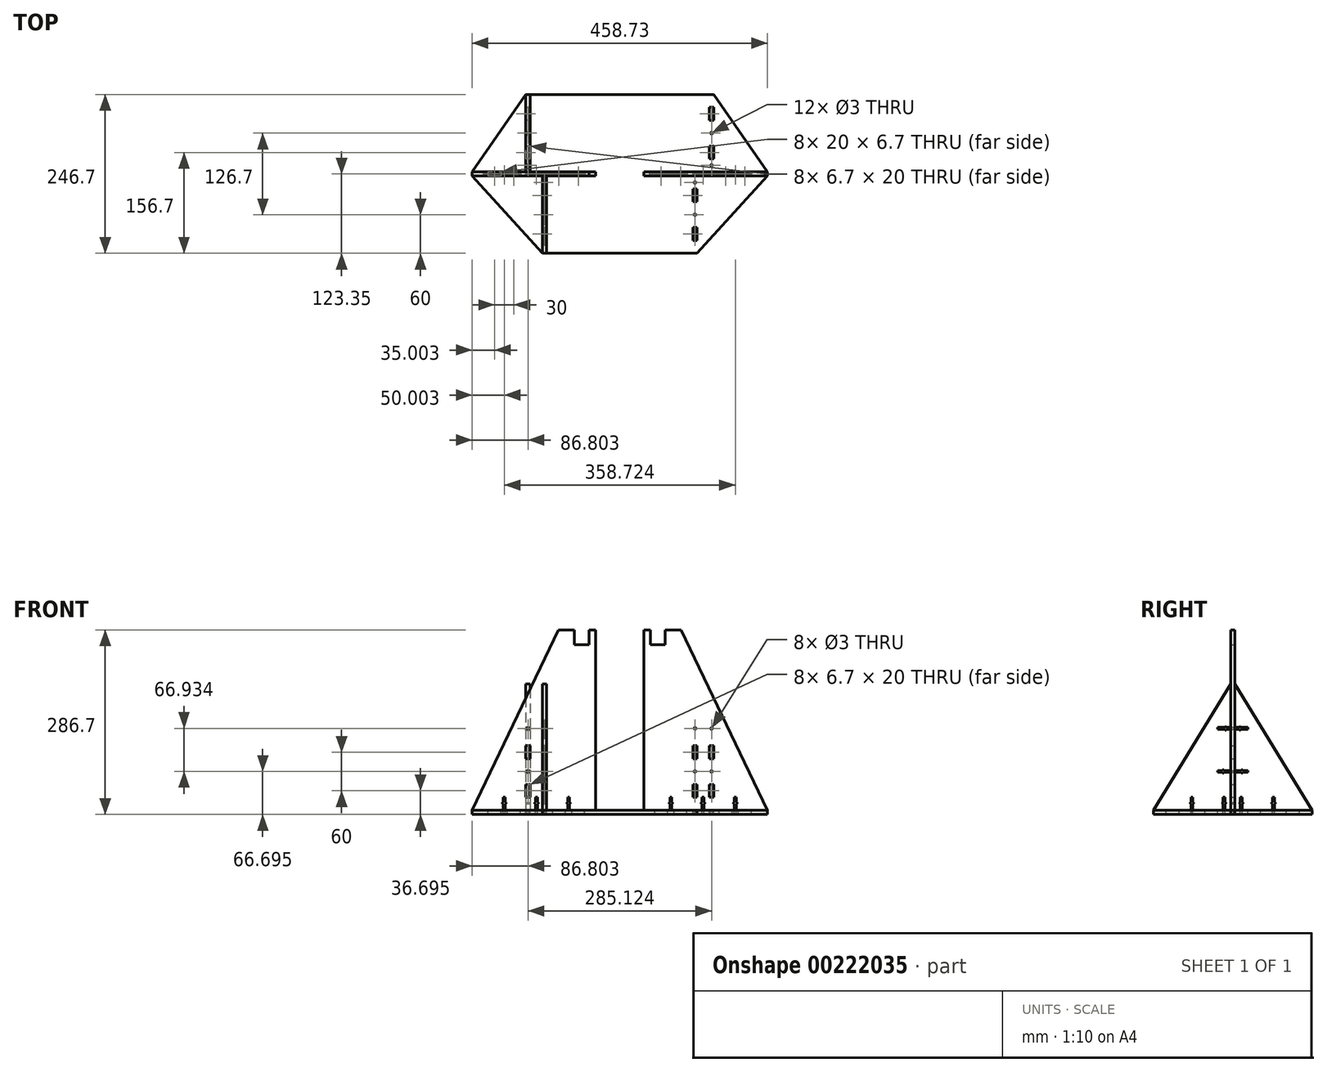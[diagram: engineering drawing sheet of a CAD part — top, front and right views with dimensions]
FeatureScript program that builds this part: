
annotation { "Feature Type Name" : "Feature", "Feature Type Description" : "" }
export const myFeature = defineFeature(function(context is Context, id is Id, definition is map)
    precondition{}
    {
        {
            var Q0;
            Q0=qCreatedBy(makeId("Front.planeOp"),FACE);
            var sketch = newSketch(context, id + "F0", { "sketchPlane" : qUnion([Q0])});
            skLineSegment(sketch, "E0", {"start": v(-65.14, 306.1) * mm, "end": v(-65.14, 283.1) * mm});
            skLineSegment(sketch, "E1", {"start": v(-65.14, 306.1) * mm, "end": v(-55.14, 306.1) * mm, "construction": true});
            skLineSegment(sketch, "E2", {"start": v(-65.14, 283.1) * mm, "end": v(-88.14, 283.1) * mm});
            skLineSegment(sketch, "E3", {"start": v(-88.14, 283.1) * mm, "end": v(-88.14, 306.1) * mm});
            skLineSegment(sketch, "E4", {"start": v(-65.14, 306.1) * mm, "end": v(-55.14, 306.1) * mm});
            skLineSegment(sketch, "E5", {"start": v(-88.14, 306.1) * mm, "end": v(-113.14, 306.1) * mm});
            skLineSegment(sketch, "E6", {"start": v(-113.14, 306.1) * mm, "end": v(-247, 26.1) * mm});
            skLineSegment(sketch, "E7", {"start": v(-247, 26.1) * mm, "end": v(-222, 26.1) * mm});
            skLineSegment(sketch, "E8.top", {"start": v(-222, 19.4) * mm, "end": v(-202, 19.4) * mm});
            skLineSegment(sketch, "E8.left", {"start": v(-222, 26.1) * mm, "end": v(-222, 19.4) * mm});
            skLineSegment(sketch, "E8.right", {"start": v(-202, 26.1) * mm, "end": v(-202, 19.4) * mm});
            skLineSegment(sketch, "E9.top", {"start": v(-192, 19.4) * mm, "end": v(-172, 19.4) * mm});
            skLineSegment(sketch, "E9.left", {"start": v(-192, 26.1) * mm, "end": v(-192, 19.4) * mm});
            skLineSegment(sketch, "E9.right", {"start": v(-172, 26.1) * mm, "end": v(-172, 19.4) * mm});
            skLineSegment(sketch, "E10.trimOffspring", {"start": v(-202, 26.1) * mm, "end": v(-198.5, 26.1) * mm});
            skLineSegment(sketch, "E11.MirrorCS", {"start": v(-122, 26.1) * mm, "end": v(-122, 19.4) * mm});
            skLineSegment(sketch, "E12.MirrorCS", {"start": v(-102, 19.4) * mm, "end": v(-122, 19.4) * mm});
            skLineSegment(sketch, "E13.MirrorCS", {"start": v(-102, 26.1) * mm, "end": v(-102, 19.4) * mm});
            skLineSegment(sketch, "E14.MirrorCS", {"start": v(-92, 26.1) * mm, "end": v(-95.5, 26.1) * mm});
            skLineSegment(sketch, "E15.MirrorCS", {"start": v(-92, 26.1) * mm, "end": v(-92, 19.4) * mm});
            skLineSegment(sketch, "E16.MirrorCS", {"start": v(-72, 26.1) * mm, "end": v(-72, 19.4) * mm});
            skLineSegment(sketch, "E17.MirrorCS", {"start": v(-72, 19.4) * mm, "end": v(-92, 19.4) * mm});
            skLineSegment(sketch, "E18", {"start": v(-72, 26.1) * mm, "end": v(-55.14, 26.1) * mm});
            skLineSegment(sketch, "E19.bottom", {"start": v(-198.5, 46.1) * mm, "end": v(-195.5, 46.1) * mm});
            skLineSegment(sketch, "E19.left", {"start": v(-198.5, 46.1) * mm, "end": v(-198.5, 37.9) * mm});
            skLineSegment(sketch, "E19.right", {"start": v(-195.5, 46.1) * mm, "end": v(-195.5, 37.9) * mm});
            skPoint(sketch, "E20.oppositeSnap0", {"position": v(-195.5, 36.1) * mm});
            skLineSegment(sketch, "E20.bottom", {"start": v(-199.76, 37.9) * mm, "end": v(-198.5, 37.9) * mm});
            skLineSegment(sketch, "E20.top", {"start": v(-199.76, 36.1) * mm, "end": v(-198.5, 36.1) * mm});
            skLineSegment(sketch, "E20.left", {"start": v(-199.76, 37.9) * mm, "end": v(-199.76, 36.1) * mm});
            skLineSegment(sketch, "E20.right", {"start": v(-194.26, 37.9) * mm, "end": v(-194.26, 36.1) * mm});
            skLineSegment(sketch, "E21.trimOffspring", {"start": v(-195.5, 36.1) * mm, "end": v(-194.26, 36.1) * mm});
            skLineSegment(sketch, "E22.trimOffspring", {"start": v(-195.5, 37.9) * mm, "end": v(-194.26, 37.9) * mm});
            skLineSegment(sketch, "E23.trimOffspring", {"start": v(-198.5, 36.1) * mm, "end": v(-198.5, 26.1) * mm});
            skLineSegment(sketch, "E24.trimOffspring", {"start": v(-195.5, 36.1) * mm, "end": v(-195.5, 26.1) * mm});
            skLineSegment(sketch, "E25.trimOffspring", {"start": v(-195.5, 26.1) * mm, "end": v(-192, 26.1) * mm});
            skLineSegment(sketch, "E26.MirrorCS", {"start": v(-95.5, 46.1) * mm, "end": v(-98.5, 46.1) * mm});
            skLineSegment(sketch, "E27.MirrorCS", {"start": v(-98.5, 46.1) * mm, "end": v(-98.5, 37.9) * mm});
            skLineSegment(sketch, "E28.MirrorCS", {"start": v(-98.5, 37.9) * mm, "end": v(-99.76, 37.9) * mm});
            skLineSegment(sketch, "E29.MirrorCS", {"start": v(-99.76, 37.9) * mm, "end": v(-99.76, 36.1) * mm});
            skLineSegment(sketch, "E30.MirrorCS", {"start": v(-98.5, 36.1) * mm, "end": v(-99.76, 36.1) * mm});
            skLineSegment(sketch, "E31.MirrorCS", {"start": v(-98.5, 36.1) * mm, "end": v(-98.5, 26.1) * mm});
            skLineSegment(sketch, "E32.MirrorCS", {"start": v(-94.26, 37.9) * mm, "end": v(-95.5, 37.9) * mm});
            skLineSegment(sketch, "E33.MirrorCS", {"start": v(-95.5, 46.1) * mm, "end": v(-95.5, 37.9) * mm});
            skLineSegment(sketch, "E34.MirrorCS", {"start": v(-94.26, 37.9) * mm, "end": v(-94.26, 36.1) * mm});
            skLineSegment(sketch, "E35.MirrorCS", {"start": v(-95.5, 36.1) * mm, "end": v(-95.5, 26.1) * mm});
            skLineSegment(sketch, "E36.MirrorCS", {"start": v(-94.26, 36.1) * mm, "end": v(-95.5, 36.1) * mm});
            skLineSegment(sketch, "E37.trimOffspring", {"start": v(-98.5, 26.1) * mm, "end": v(-102, 26.1) * mm});
            skLineSegment(sketch, "E38.bottom", {"start": v(-163.56, 126.1) * mm, "end": v(-156.86, 126.1) * mm, "construction": true});
            skLineSegment(sketch, "E39.bottom", {"start": v(-163.56, 126.1) * mm, "end": v(-156.86, 126.1) * mm});
            skLineSegment(sketch, "E39.top", {"start": v(-163.56, 106.1) * mm, "end": v(-156.86, 106.1) * mm});
            skLineSegment(sketch, "E39.left", {"start": v(-163.56, 126.1) * mm, "end": v(-163.56, 106.1) * mm});
            skLineSegment(sketch, "E39.right", {"start": v(-156.86, 126.1) * mm, "end": v(-156.86, 106.1) * mm});
            skLineSegment(sketch, "E40.bottom", {"start": v(-156.86, 66.1) * mm, "end": v(-163.56, 66.1) * mm});
            skLineSegment(sketch, "E40.top", {"start": v(-156.86, 46.1) * mm, "end": v(-163.56, 46.1) * mm});
            skLineSegment(sketch, "E40.left", {"start": v(-156.86, 66.1) * mm, "end": v(-156.86, 46.1) * mm});
            skLineSegment(sketch, "E40.right", {"start": v(-163.56, 66.1) * mm, "end": v(-163.56, 46.1) * mm});
            skCircle(sketch, "E41", {"center": v(-160.2, 86.1) * mm, "radius": 1.5 * mm});
            skLineSegment(sketch, "E42.bottom", {"start": v(-137.86, 126.1) * mm, "end": v(-131.16, 126.1) * mm});
            skLineSegment(sketch, "E42.top", {"start": v(-137.86, 106.1) * mm, "end": v(-131.16, 106.1) * mm});
            skLineSegment(sketch, "E42.left", {"start": v(-137.86, 126.1) * mm, "end": v(-137.86, 106.1) * mm});
            skLineSegment(sketch, "E42.right", {"start": v(-131.16, 126.1) * mm, "end": v(-131.16, 106.1) * mm});
            skCircle(sketch, "E43", {"center": v(-134.5, 86.1) * mm, "radius": 1.5 * mm});
            skLineSegment(sketch, "E44.bottom", {"start": v(-137.86, 66.1) * mm, "end": v(-131.16, 66.1) * mm});
            skLineSegment(sketch, "E44.top", {"start": v(-137.86, 46.1) * mm, "end": v(-131.16, 46.1) * mm});
            skLineSegment(sketch, "E44.left", {"start": v(-137.86, 66.1) * mm, "end": v(-137.86, 46.1) * mm});
            skLineSegment(sketch, "E44.right", {"start": v(-131.16, 66.1) * mm, "end": v(-131.16, 46.1) * mm});
            skLineSegment(sketch, "E45", {"start": v(-122, 26.1) * mm, "end": v(-145.5, 26.1) * mm});
            skLineSegment(sketch, "E46.bottom", {"start": v(-148.5, 46.1) * mm, "end": v(-145.5, 46.1) * mm});
            skLineSegment(sketch, "E46.left", {"start": v(-148.5, 46.1) * mm, "end": v(-148.5, 37.9) * mm});
            skLineSegment(sketch, "E46.right", {"start": v(-145.5, 46.1) * mm, "end": v(-145.5, 37.9) * mm});
            skLineSegment(sketch, "E47.bottom", {"start": v(-149.76, 37.9) * mm, "end": v(-148.5, 37.9) * mm});
            skLineSegment(sketch, "E47.top", {"start": v(-149.76, 36.1) * mm, "end": v(-148.5, 36.1) * mm});
            skLineSegment(sketch, "E47.left", {"start": v(-149.76, 37.9) * mm, "end": v(-149.76, 36.1) * mm});
            skLineSegment(sketch, "E47.right", {"start": v(-144.26, 37.9) * mm, "end": v(-144.26, 36.1) * mm});
            skLineSegment(sketch, "E48.trimOffspring", {"start": v(-145.5, 36.1) * mm, "end": v(-144.26, 36.1) * mm});
            skLineSegment(sketch, "E49.trimOffspring", {"start": v(-148.5, 36.1) * mm, "end": v(-148.5, 26.1) * mm});
            skLineSegment(sketch, "E50.trimOffspring", {"start": v(-145.5, 37.9) * mm, "end": v(-144.26, 37.9) * mm});
            skLineSegment(sketch, "E51.trimOffspring", {"start": v(-145.5, 36.1) * mm, "end": v(-145.5, 26.1) * mm});
            skLineSegment(sketch, "E52.trimOffspring", {"start": v(-148.5, 26.1) * mm, "end": v(-172, 26.1) * mm});
            skLineSegment(sketch, "E53.MirrorCS", {"start": v(158.97, 37.9) * mm, "end": v(158.97, 36.1) * mm});
            skLineSegment(sketch, "E54.MirrorCS", {"start": v(164.47, 37.9) * mm, "end": v(163.22, 37.9) * mm});
            skLineSegment(sketch, "E55.MirrorCS", {"start": v(160.22, 36.1) * mm, "end": v(158.97, 36.1) * mm});
            skLineSegment(sketch, "E56.MirrorCS", {"start": v(164.47, 37.9) * mm, "end": v(164.47, 36.1) * mm});
            skLineSegment(sketch, "E57.MirrorCS", {"start": v(160.22, 37.9) * mm, "end": v(158.97, 37.9) * mm});
            skLineSegment(sketch, "E58.MirrorCS", {"start": v(164.47, 36.1) * mm, "end": v(163.22, 36.1) * mm});
            skLineSegment(sketch, "E59.MirrorCS", {"start": v(63.22, 37.9) * mm, "end": v(64.47, 37.9) * mm});
            skLineSegment(sketch, "E60.MirrorCS", {"start": v(63.22, 36.1) * mm, "end": v(64.47, 36.1) * mm});
            skLineSegment(sketch, "E61.MirrorCS", {"start": v(64.47, 37.9) * mm, "end": v(64.47, 36.1) * mm});
            skLineSegment(sketch, "E62.MirrorCS", {"start": v(58.97, 36.1) * mm, "end": v(60.22, 36.1) * mm});
            skLineSegment(sketch, "E63.MirrorCS", {"start": v(58.97, 37.9) * mm, "end": v(58.97, 36.1) * mm});
            skLineSegment(sketch, "E64.MirrorCS", {"start": v(58.97, 37.9) * mm, "end": v(60.22, 37.9) * mm});
            skLineSegment(sketch, "E65.MirrorCS", {"start": v(108.97, 37.9) * mm, "end": v(108.97, 36.1) * mm});
            skLineSegment(sketch, "E66.MirrorCS", {"start": v(114.47, 36.1) * mm, "end": v(113.22, 36.1) * mm});
            skLineSegment(sketch, "E67.MirrorCS", {"start": v(114.47, 37.9) * mm, "end": v(113.22, 37.9) * mm});
            skLineSegment(sketch, "E68.MirrorCS", {"start": v(110.22, 37.9) * mm, "end": v(108.97, 37.9) * mm});
            skLineSegment(sketch, "E69.MirrorCS", {"start": v(110.22, 36.1) * mm, "end": v(108.97, 36.1) * mm});
            skLineSegment(sketch, "E70.MirrorCS", {"start": v(114.47, 37.9) * mm, "end": v(114.47, 36.1) * mm});
            skLineSegment(sketch, "E71.MirrorCS", {"start": v(160.22, 26.1) * mm, "end": v(156.72, 26.1) * mm});
            skLineSegment(sketch, "E72.MirrorCS", {"start": v(56.72, 26.1) * mm, "end": v(60.22, 26.1) * mm});
            skLineSegment(sketch, "E73.MirrorCS", {"start": v(166.72, 26.1) * mm, "end": v(163.22, 26.1) * mm});
            skLineSegment(sketch, "E74.MirrorCS", {"start": v(128.27, 126.1) * mm, "end": v(121.57, 126.1) * mm});
            skLineSegment(sketch, "E75.MirrorCS", {"start": v(63.22, 26.1) * mm, "end": v(66.72, 26.1) * mm});
            skLineSegment(sketch, "E76.MirrorCS", {"start": v(156.72, 26.1) * mm, "end": v(156.72, 19.4) * mm});
            skLineSegment(sketch, "E77.MirrorCS", {"start": v(66.72, 26.1) * mm, "end": v(66.72, 19.4) * mm});
            skLineSegment(sketch, "E78.MirrorCS", {"start": v(63.22, 36.1) * mm, "end": v(63.22, 26.1) * mm});
            skLineSegment(sketch, "E79.MirrorCS", {"start": v(29.86, 306.1) * mm, "end": v(19.86, 306.1) * mm, "construction": true});
            skLineSegment(sketch, "E80.MirrorCS", {"start": v(128.27, 126.1) * mm, "end": v(121.57, 126.1) * mm, "construction": true});
            skLineSegment(sketch, "E81.MirrorCS", {"start": v(166.72, 26.1) * mm, "end": v(166.72, 19.4) * mm});
            skLineSegment(sketch, "E82.MirrorCS", {"start": v(110.22, 46.1) * mm, "end": v(110.22, 37.9) * mm});
            skLineSegment(sketch, "E83.MirrorCS", {"start": v(56.72, 26.1) * mm, "end": v(56.72, 19.4) * mm});
            skLineSegment(sketch, "E84.MirrorCS", {"start": v(160.22, 36.1) * mm, "end": v(160.22, 26.1) * mm});
            skLineSegment(sketch, "E85.MirrorCS", {"start": v(60.22, 36.1) * mm, "end": v(60.22, 26.1) * mm});
            skLineSegment(sketch, "E86.MirrorCS", {"start": v(113.22, 46.1) * mm, "end": v(110.22, 46.1) * mm});
            skLineSegment(sketch, "E87.MirrorCS", {"start": v(163.22, 36.1) * mm, "end": v(163.22, 26.1) * mm});
            skLineSegment(sketch, "E88.MirrorCS", {"start": v(113.22, 46.1) * mm, "end": v(113.22, 37.9) * mm});
            skLineSegment(sketch, "E89.MirrorCS", {"start": v(128.27, 106.1) * mm, "end": v(121.57, 106.1) * mm});
            skLineSegment(sketch, "E90.MirrorCS", {"start": v(121.57, 46.1) * mm, "end": v(128.27, 46.1) * mm});
            skLineSegment(sketch, "E91.MirrorCS", {"start": v(160.22, 46.1) * mm, "end": v(160.22, 37.9) * mm});
            skLineSegment(sketch, "E92.MirrorCS", {"start": v(102.57, 126.1) * mm, "end": v(95.87, 126.1) * mm});
            skLineSegment(sketch, "E93.MirrorCS", {"start": v(163.22, 46.1) * mm, "end": v(163.22, 37.9) * mm});
            skLineSegment(sketch, "E94.MirrorCS", {"start": v(136.72, 26.1) * mm, "end": v(136.72, 19.4) * mm});
            skLineSegment(sketch, "E95.MirrorCS", {"start": v(163.22, 46.1) * mm, "end": v(160.22, 46.1) * mm});
            skLineSegment(sketch, "E96.MirrorCS", {"start": v(86.72, 26.1) * mm, "end": v(86.72, 19.4) * mm});
            skLineSegment(sketch, "E97.MirrorCS", {"start": v(186.72, 26.1) * mm, "end": v(186.72, 19.4) * mm});
            skLineSegment(sketch, "E98.MirrorCS", {"start": v(110.22, 36.1) * mm, "end": v(110.22, 26.1) * mm});
            skLineSegment(sketch, "E99.MirrorCS", {"start": v(121.57, 66.1) * mm, "end": v(128.27, 66.1) * mm});
            skLineSegment(sketch, "E100.MirrorCS", {"start": v(102.57, 106.1) * mm, "end": v(95.87, 106.1) * mm});
            skLineSegment(sketch, "E101.MirrorCS", {"start": v(102.57, 66.1) * mm, "end": v(95.87, 66.1) * mm});
            skLineSegment(sketch, "E102.MirrorCS", {"start": v(60.22, 46.1) * mm, "end": v(63.22, 46.1) * mm});
            skLineSegment(sketch, "E103.MirrorCS", {"start": v(102.57, 46.1) * mm, "end": v(95.87, 46.1) * mm});
            skLineSegment(sketch, "E104.MirrorCS", {"start": v(113.22, 36.1) * mm, "end": v(113.22, 26.1) * mm});
            skLineSegment(sketch, "E105.MirrorCS", {"start": v(60.22, 46.1) * mm, "end": v(60.22, 37.9) * mm});
            skLineSegment(sketch, "E106.MirrorCS", {"start": v(36.72, 26.1) * mm, "end": v(36.72, 19.4) * mm});
            skLineSegment(sketch, "E107.MirrorCS", {"start": v(63.22, 46.1) * mm, "end": v(63.22, 37.9) * mm});
            skCircle(sketch, "E108.MirrorC", {"center": v(124.92, 86.1) * mm, "radius": 1.5 * mm});
            skLineSegment(sketch, "E109.MirrorCS", {"start": v(29.86, 306.1) * mm, "end": v(19.86, 306.1) * mm});
            skCircle(sketch, "E110.MirrorC", {"center": v(99.22, 86.1) * mm, "radius": 1.5 * mm});
            skLineSegment(sketch, "E111.MirrorCS", {"start": v(156.72, 19.4) * mm, "end": v(136.72, 19.4) * mm});
            skLineSegment(sketch, "E112.MirrorCS", {"start": v(95.87, 126.1) * mm, "end": v(95.87, 106.1) * mm});
            skLineSegment(sketch, "E113.MirrorCS", {"start": v(128.27, 126.1) * mm, "end": v(128.27, 106.1) * mm});
            skLineSegment(sketch, "E114.MirrorCS", {"start": v(95.87, 66.1) * mm, "end": v(95.87, 46.1) * mm});
            skLineSegment(sketch, "E115.MirrorCS", {"start": v(29.86, 306.1) * mm, "end": v(29.86, 283.1) * mm});
            skLineSegment(sketch, "E116.MirrorCS", {"start": v(102.57, 66.1) * mm, "end": v(102.57, 46.1) * mm});
            skLineSegment(sketch, "E117.MirrorCS", {"start": v(29.86, 283.1) * mm, "end": v(52.86, 283.1) * mm});
            skLineSegment(sketch, "E118.MirrorCS", {"start": v(128.27, 66.1) * mm, "end": v(128.27, 46.1) * mm});
            skLineSegment(sketch, "E119.MirrorCS", {"start": v(52.86, 283.1) * mm, "end": v(52.86, 306.1) * mm});
            skLineSegment(sketch, "E120.MirrorCS", {"start": v(52.86, 306.1) * mm, "end": v(77.86, 306.1) * mm});
            skLineSegment(sketch, "E121.MirrorCS", {"start": v(77.86, 306.1) * mm, "end": v(211.72, 26.1) * mm});
            skLineSegment(sketch, "E122.MirrorCS", {"start": v(211.72, 26.1) * mm, "end": v(186.72, 26.1) * mm});
            skLineSegment(sketch, "E123.MirrorCS", {"start": v(121.57, 66.1) * mm, "end": v(121.57, 46.1) * mm});
            skLineSegment(sketch, "E124.MirrorCS", {"start": v(36.72, 26.1) * mm, "end": v(19.86, 26.1) * mm});
            skLineSegment(sketch, "E125.MirrorCS", {"start": v(66.72, 19.4) * mm, "end": v(86.72, 19.4) * mm});
            skLineSegment(sketch, "E126.MirrorCS", {"start": v(36.72, 19.4) * mm, "end": v(56.72, 19.4) * mm});
            skLineSegment(sketch, "E127.MirrorCS", {"start": v(113.22, 26.1) * mm, "end": v(136.72, 26.1) * mm});
            skLineSegment(sketch, "E128.MirrorCS", {"start": v(121.57, 126.1) * mm, "end": v(121.57, 106.1) * mm});
            skPoint(sketch, "E129.MirrorP", {"position": v(160.22, 36.1) * mm});
            skLineSegment(sketch, "E130.MirrorCS", {"start": v(186.72, 19.4) * mm, "end": v(166.72, 19.4) * mm});
            skLineSegment(sketch, "E131.MirrorCS", {"start": v(102.57, 126.1) * mm, "end": v(102.57, 106.1) * mm});
            skLineSegment(sketch, "E132.MirrorCS", {"start": v(86.72, 26.1) * mm, "end": v(110.22, 26.1) * mm});
            skPoint(sketch, "E133.endSnap0", {"position": v(-58.58, 26.1) * mm});
            skLineSegment(sketch, "E134", {"start": v(-55.14, 306.1) * mm, "end": v(-55.14, 26.1) * mm});
            skLineSegment(sketch, "E135.trimOffspring", {"start": v(-55.14, 306.1) * mm, "end": v(-65.14, 306.1) * mm, "construction": true});
            skLineSegment(sketch, "E136", {"start": v(19.86, 306.1) * mm, "end": v(19.86, 26.1) * mm});
            skPoint(sketch, "E136.startSnap0", {"position": v(19.86, 306.1) * mm});
            skLineSegment(sketch, "E137.trimOffspring", {"start": v(19.86, 306.1) * mm, "end": v(29.86, 306.1) * mm, "construction": true});
            skPoint(sketch, "E138.orphan", {"position": v(19.86, 315.9) * mm});
            skPoint(sketch, "E139.trimOffspring.start.orphan", {"position": v(9.86, 306.1) * mm});
            skSolve(sketch);
        }
        {
            var Q0;
            Q0 = qSketchRegion(id + "F0", true);
            extrude(context, id + "F1", {"entities" : qUnion([Q0]), "depth" : 6.7 * mm});
        }
        {
            var Q0;
            Q0=makeQuery(id+"F1.opExtrude","SWEPT_FACE",FACE,{"disambiguationData":[OSD([sQuery(id+"F0.wireOp",EDGE,"E42.right")])]});
            var sketch = newSketch(context, id + "F2", { "sketchPlane" : qUnion([Q0])});
            skLineSegment(sketch, "E140.0", {"start": v(0, 126.1) * mm, "end": v(0, 106.1) * mm});
            skLineSegment(sketch, "E141.0", {"start": v(6.7, 106.1) * mm, "end": v(0, 106.1) * mm});
            skLineSegment(sketch, "E142.0", {"start": v(6.7, 126.1) * mm, "end": v(0, 126.1) * mm});
            skLineSegment(sketch, "E143.0", {"start": v(6.7, 66.1) * mm, "end": v(0, 66.1) * mm});
            skLineSegment(sketch, "E144.0", {"start": v(0, 66.1) * mm, "end": v(0, 46.1) * mm});
            skLineSegment(sketch, "E145.0", {"start": v(6.7, 46.1) * mm, "end": v(0, 46.1) * mm});
            skLineSegment(sketch, "E146.0", {"start": v(6.7, 26.1) * mm, "end": v(0, 26.1) * mm, "construction": true});
            skLineSegment(sketch, "E147", {"start": v(6.7, 106.1) * mm, "end": v(6.7, 87.6) * mm});
            skLineSegment(sketch, "E148", {"start": v(6.7, 46.1) * mm, "end": v(6.7, 26.1) * mm});
            skLineSegment(sketch, "E149", {"start": v(6.7, 222.2) * mm, "end": v(126.7, 26.1) * mm});
            skLineSegment(sketch, "E150", {"start": v(126.7, 26.1) * mm, "end": v(106.7, 26.1) * mm});
            skLineSegment(sketch, "E151.0", {"start": v(6.7, 19.4) * mm, "end": v(0, 19.4) * mm, "construction": true});
            skLineSegment(sketch, "E152.top", {"start": v(26.7, 19.4) * mm, "end": v(46.7, 19.4) * mm});
            skLineSegment(sketch, "E152.left", {"start": v(26.7, 26.1) * mm, "end": v(26.7, 19.4) * mm});
            skLineSegment(sketch, "E152.right", {"start": v(46.7, 26.1) * mm, "end": v(46.7, 19.4) * mm});
            skLineSegment(sketch, "E153.trimOffspring", {"start": v(26.7, 26.1) * mm, "end": v(18.2, 26.1) * mm});
            skLineSegment(sketch, "E154.top", {"start": v(86.7, 19.4) * mm, "end": v(106.7, 19.4) * mm});
            skLineSegment(sketch, "E154.left", {"start": v(86.7, 26.1) * mm, "end": v(86.7, 19.4) * mm});
            skLineSegment(sketch, "E154.right", {"start": v(106.7, 26.1) * mm, "end": v(106.7, 19.4) * mm});
            skLineSegment(sketch, "E155.trimOffspring", {"start": v(86.7, 26.1) * mm, "end": v(68.2, 26.1) * mm});
            skLineSegment(sketch, "E156.bottom", {"start": v(18.2, 46.1) * mm, "end": v(15.2, 46.1) * mm});
            skLineSegment(sketch, "E156.left", {"start": v(18.2, 46.1) * mm, "end": v(18.2, 37.9) * mm});
            skLineSegment(sketch, "E156.right", {"start": v(15.2, 46.1) * mm, "end": v(15.2, 37.9) * mm});
            skLineSegment(sketch, "E157.bottom", {"start": v(19.45, 37.9) * mm, "end": v(18.2, 37.9) * mm});
            skLineSegment(sketch, "E157.top", {"start": v(19.45, 36.1) * mm, "end": v(18.2, 36.1) * mm});
            skLineSegment(sketch, "E157.left", {"start": v(19.45, 37.9) * mm, "end": v(19.45, 36.1) * mm});
            skLineSegment(sketch, "E157.right", {"start": v(13.95, 37.9) * mm, "end": v(13.95, 36.1) * mm});
            skLineSegment(sketch, "E158.trimOffspring", {"start": v(15.2, 36.1) * mm, "end": v(13.95, 36.1) * mm});
            skLineSegment(sketch, "E159.trimOffspring", {"start": v(15.2, 37.9) * mm, "end": v(13.95, 37.9) * mm});
            skLineSegment(sketch, "E160.trimOffspring", {"start": v(15.2, 36.1) * mm, "end": v(15.2, 26.1) * mm});
            skLineSegment(sketch, "E161.trimOffspring", {"start": v(18.2, 36.1) * mm, "end": v(18.2, 26.1) * mm});
            skLineSegment(sketch, "E162.trimOffspring", {"start": v(15.2, 26.1) * mm, "end": v(6.7, 26.1) * mm});
            skLineSegment(sketch, "E163.top", {"start": v(65.2, 46.1) * mm, "end": v(68.2, 46.1) * mm});
            skLineSegment(sketch, "E163.left", {"start": v(65.2, 26.1) * mm, "end": v(65.2, 36.1) * mm});
            skLineSegment(sketch, "E163.right", {"start": v(68.2, 26.1) * mm, "end": v(68.2, 36.1) * mm});
            skLineSegment(sketch, "E164.bottom", {"start": v(63.95, 37.9) * mm, "end": v(65.2, 37.9) * mm});
            skLineSegment(sketch, "E164.top", {"start": v(63.95, 36.1) * mm, "end": v(65.2, 36.1) * mm});
            skLineSegment(sketch, "E164.left", {"start": v(63.95, 37.9) * mm, "end": v(63.95, 36.1) * mm});
            skLineSegment(sketch, "E164.right", {"start": v(69.45, 37.9) * mm, "end": v(69.45, 36.1) * mm});
            skLineSegment(sketch, "E165.trimOffspring", {"start": v(68.2, 36.1) * mm, "end": v(69.45, 36.1) * mm});
            skLineSegment(sketch, "E166.trimOffspring", {"start": v(65.2, 37.9) * mm, "end": v(65.2, 46.1) * mm});
            skLineSegment(sketch, "E167.trimOffspring", {"start": v(68.2, 37.9) * mm, "end": v(69.45, 37.9) * mm});
            skLineSegment(sketch, "E168.trimOffspring", {"start": v(68.2, 37.9) * mm, "end": v(68.2, 46.1) * mm});
            skLineSegment(sketch, "E169.trimOffspring", {"start": v(65.2, 26.1) * mm, "end": v(46.7, 26.1) * mm});
            skLineSegment(sketch, "E170.bottom", {"start": v(6.7, 87.6) * mm, "end": v(17.09, 87.6) * mm});
            skLineSegment(sketch, "E170.top", {"start": v(6.7, 84.6) * mm, "end": v(17.09, 84.6) * mm});
            skLineSegment(sketch, "E170.right", {"start": v(26.7, 87.6) * mm, "end": v(26.7, 84.6) * mm});
            skLineSegment(sketch, "E171.bottom", {"start": v(17.09, 88.86) * mm, "end": v(18.89, 88.86) * mm});
            skLineSegment(sketch, "E171.top", {"start": v(17.09, 83.36) * mm, "end": v(18.89, 83.36) * mm});
            skLineSegment(sketch, "E171.left", {"start": v(17.09, 88.86) * mm, "end": v(17.09, 87.6) * mm});
            skLineSegment(sketch, "E171.right", {"start": v(18.89, 88.86) * mm, "end": v(18.89, 87.6) * mm});
            skLineSegment(sketch, "E172.trimOffspring", {"start": v(18.89, 87.6) * mm, "end": v(26.7, 87.6) * mm});
            skLineSegment(sketch, "E173.trimOffspring", {"start": v(17.09, 84.6) * mm, "end": v(17.09, 83.36) * mm});
            skLineSegment(sketch, "E174.trimOffspring", {"start": v(18.89, 84.6) * mm, "end": v(18.89, 83.36) * mm});
            skLineSegment(sketch, "E175.trimOffspring", {"start": v(18.89, 84.6) * mm, "end": v(26.7, 84.6) * mm});
            skLineSegment(sketch, "E176.trimOffspring", {"start": v(6.7, 84.6) * mm, "end": v(6.7, 66.1) * mm});
            skLineSegment(sketch, "E177.bottom", {"start": v(6.7, 154.54) * mm, "end": v(13.45, 154.54) * mm});
            skLineSegment(sketch, "E177.top", {"start": v(6.7, 151.54) * mm, "end": v(13.45, 151.54) * mm});
            skLineSegment(sketch, "E177.right", {"start": v(26.7, 154.54) * mm, "end": v(26.7, 151.54) * mm});
            skLineSegment(sketch, "E178.bottom", {"start": v(13.45, 155.62) * mm, "end": v(15.25, 155.62) * mm});
            skLineSegment(sketch, "E178.top", {"start": v(13.45, 150.12) * mm, "end": v(15.25, 150.12) * mm});
            skLineSegment(sketch, "E178.left", {"start": v(13.45, 155.62) * mm, "end": v(13.45, 154.54) * mm});
            skLineSegment(sketch, "E178.right", {"start": v(15.25, 155.62) * mm, "end": v(15.25, 154.54) * mm});
            skLineSegment(sketch, "E179.trimOffspring", {"start": v(13.45, 151.54) * mm, "end": v(13.45, 150.12) * mm});
            skLineSegment(sketch, "E180.trimOffspring", {"start": v(15.25, 154.54) * mm, "end": v(26.7, 154.54) * mm});
            skLineSegment(sketch, "E181.trimOffspring", {"start": v(15.25, 151.54) * mm, "end": v(15.25, 150.12) * mm});
            skLineSegment(sketch, "E182.trimOffspring", {"start": v(15.25, 151.54) * mm, "end": v(26.7, 151.54) * mm});
            skLineSegment(sketch, "E183.trimOffspring", {"start": v(6.7, 151.54) * mm, "end": v(6.7, 126.1) * mm});
            skLineSegment(sketch, "E184", {"start": v(6.7, 154.54) * mm, "end": v(6.7, 222.2) * mm});
            skSolve(sketch);
        }
        {
            var Q0;
            Q0 = qSketchRegion(id + "F2", true);
            extrude(context, id + "F3", {"entities" : qUnion([Q0]), "depth" : 6.7 * mm});
        }
        {
            var Q0;
            Q0=makeQuery(id+"F1.opExtrude","CAP_FACE",FACE,{"disambiguationData":[OSD([sQuery(id+"F0.wireOp",EDGE,"E0"),sQuery(id+"F0.wireOp",EDGE,"E2"),sQuery(id+"F0.wireOp",EDGE,"E3"),sQuery(id+"F0.wireOp",EDGE,"E4"),sQuery(id+"F0.wireOp",EDGE,"QfhwlkQs-FwJa-Vd4a-oDgf-JxR3PnwzFohU"),sQuery(id+"F0.wireOp",EDGE,"E5"),sQuery(id+"F0.wireOp",EDGE,"E6"),sQuery(id+"F0.wireOp",EDGE,"E7"),sQuery(id+"F0.wireOp",EDGE,"E8.top"),sQuery(id+"F0.wireOp",EDGE,"E8.left"),sQuery(id+"F0.wireOp",EDGE,"E8.right"),sQuery(id+"F0.wireOp",EDGE,"E9.top"),sQuery(id+"F0.wireOp",EDGE,"E9.left"),sQuery(id+"F0.wireOp",EDGE,"E9.right"),sQuery(id+"F0.wireOp",EDGE,"E10.trimOffspring"),sQuery(id+"F0.wireOp",EDGE,"E11.MirrorCS"),sQuery(id+"F0.wireOp",EDGE,"E12.MirrorCS"),sQuery(id+"F0.wireOp",EDGE,"E13.MirrorCS"),sQuery(id+"F0.wireOp",EDGE,"E14.MirrorCS"),sQuery(id+"F0.wireOp",EDGE,"E15.MirrorCS"),sQuery(id+"F0.wireOp",EDGE,"E16.MirrorCS"),sQuery(id+"F0.wireOp",EDGE,"E17.MirrorCS"),sQuery(id+"F0.wireOp",EDGE,"E18"),sQuery(id+"F0.wireOp",EDGE,"E19.bottom"),sQuery(id+"F0.wireOp",EDGE,"E19.left"),sQuery(id+"F0.wireOp",EDGE,"E19.right"),sQuery(id+"F0.wireOp",EDGE,"E20.bottom"),sQuery(id+"F0.wireOp",EDGE,"E20.top"),sQuery(id+"F0.wireOp",EDGE,"E20.left"),sQuery(id+"F0.wireOp",EDGE,"E20.right"),sQuery(id+"F0.wireOp",EDGE,"E21.trimOffspring"),sQuery(id+"F0.wireOp",EDGE,"E22.trimOffspring"),sQuery(id+"F0.wireOp",EDGE,"E23.trimOffspring"),sQuery(id+"F0.wireOp",EDGE,"E24.trimOffspring"),sQuery(id+"F0.wireOp",EDGE,"E25.trimOffspring"),sQuery(id+"F0.wireOp",EDGE,"E26.MirrorCS"),sQuery(id+"F0.wireOp",EDGE,"E27.MirrorCS"),sQuery(id+"F0.wireOp",EDGE,"E28.MirrorCS"),sQuery(id+"F0.wireOp",EDGE,"E29.MirrorCS"),sQuery(id+"F0.wireOp",EDGE,"E30.MirrorCS"),sQuery(id+"F0.wireOp",EDGE,"E31.MirrorCS"),sQuery(id+"F0.wireOp",EDGE,"E32.MirrorCS"),sQuery(id+"F0.wireOp",EDGE,"E33.MirrorCS"),sQuery(id+"F0.wireOp",EDGE,"E34.MirrorCS"),sQuery(id+"F0.wireOp",EDGE,"E35.MirrorCS"),sQuery(id+"F0.wireOp",EDGE,"E36.MirrorCS"),sQuery(id+"F0.wireOp",EDGE,"E37.trimOffspring"),sQuery(id+"F0.wireOp",EDGE,"E39.bottom"),sQuery(id+"F0.wireOp",EDGE,"E39.top"),sQuery(id+"F0.wireOp",EDGE,"E39.left"),sQuery(id+"F0.wireOp",EDGE,"E39.right"),sQuery(id+"F0.wireOp",EDGE,"E40.bottom"),sQuery(id+"F0.wireOp",EDGE,"E40.top"),sQuery(id+"F0.wireOp",EDGE,"E40.left"),sQuery(id+"F0.wireOp",EDGE,"E40.right"),sQuery(id+"F0.wireOp",EDGE,"E41"),sQuery(id+"F0.wireOp",EDGE,"E42.bottom"),sQuery(id+"F0.wireOp",EDGE,"E42.top"),sQuery(id+"F0.wireOp",EDGE,"E42.left"),sQuery(id+"F0.wireOp",EDGE,"E42.right"),sQuery(id+"F0.wireOp",EDGE,"E43"),sQuery(id+"F0.wireOp",EDGE,"E44.bottom"),sQuery(id+"F0.wireOp",EDGE,"E44.top"),sQuery(id+"F0.wireOp",EDGE,"E44.left"),sQuery(id+"F0.wireOp",EDGE,"E44.right"),sQuery(id+"F0.wireOp",EDGE,"E45"),sQuery(id+"F0.wireOp",EDGE,"E46.bottom"),sQuery(id+"F0.wireOp",EDGE,"E46.left"),sQuery(id+"F0.wireOp",EDGE,"E46.right"),sQuery(id+"F0.wireOp",EDGE,"E47.bottom"),sQuery(id+"F0.wireOp",EDGE,"E47.top"),sQuery(id+"F0.wireOp",EDGE,"E47.left"),sQuery(id+"F0.wireOp",EDGE,"E47.right"),sQuery(id+"F0.wireOp",EDGE,"E48.trimOffspring"),sQuery(id+"F0.wireOp",EDGE,"E49.trimOffspring"),sQuery(id+"F0.wireOp",EDGE,"E50.trimOffspring"),sQuery(id+"F0.wireOp",EDGE,"E51.trimOffspring"),sQuery(id+"F0.wireOp",EDGE,"E52.trimOffspring")])],"isStart":true});
            var sketch = newSketch(context, id + "F4", { "sketchPlane" : qUnion([Q0])});
            skLineSegment(sketch, "E185.0", {"start": v(137.86, 154.54) * mm, "end": v(131.16, 154.54) * mm, "construction": true});
            skLineSegment(sketch, "E186.0", {"start": v(137.86, 151.54) * mm, "end": v(131.16, 151.54) * mm, "construction": true});
            skLineSegment(sketch, "E187", {"start": v(134.5, 151.54) * mm, "end": v(134.5, 154.54) * mm, "construction": true});
            skCircle(sketch, "E188", {"center": v(134.5, 153.04) * mm, "radius": 1.5 * mm});
            skCircle(sketch, "E189.0", {"center": v(160.2, 86.1) * mm, "radius": 1.5 * mm, "construction": true});
            skLineSegment(sketch, "E190", {"start": v(160.2, 86.1) * mm, "end": v(160.2, 153.04) * mm, "construction": true});
            skCircle(sketch, "E191", {"center": v(160.2, 153.04) * mm, "radius": 1.5 * mm});
            skPoint(sketch, "E192.0", {"position": v(-99.22, 126.1) * mm});
            skLineSegment(sketch, "E193.0", {"start": v(-102.57, 126.1) * mm, "end": v(-95.87, 126.1) * mm, "construction": true});
            skLineSegment(sketch, "E194.0", {"start": v(-128.27, 126.1) * mm, "end": v(-121.57, 126.1) * mm, "construction": true});
            skCircle(sketch, "E195", {"center": v(-99.22, 153.04) * mm, "radius": 1.5 * mm});
            skCircle(sketch, "E196", {"center": v(-124.92, 153.04) * mm, "radius": 1.5 * mm});
            skPoint(sketch, "E196.centerSnap0", {"position": v(-124.92, 126.1) * mm});
            skSolve(sketch);
        }
        {
            var Q0;
            Q0 = qSketchRegion(id + "F4", true);
            extrude(context, id + "F5", {"entities" : qUnion([Q0]), "operationType" : NewBodyOperationType.REMOVE, "oppositeDirection" : true, "depth" : 25 * mm});
        }
        {
            var Q0;
            Q0=makeQuery(id+"F1.opExtrude","SWEPT_FACE",FACE,{"disambiguationData":[OSD([sQuery(id+"F0.wireOp",EDGE,"E39.right")])]});
            var sketch = newSketch(context, id + "F6", { "sketchPlane" : qUnion([Q0])});
            skLineSegment(sketch, "E197.0.0", {"start": v(6.7, 126.1) * mm, "end": v(0, 126.1) * mm});
            skLineSegment(sketch, "E197.0.2", {"start": v(0, 106.1) * mm, "end": v(6.7, 106.1) * mm});
            skLineSegment(sketch, "E197.0.16", {"start": v(6.7, 66.1) * mm, "end": v(0, 66.1) * mm});
            skLineSegment(sketch, "E197.0.18", {"start": v(0, 46.1) * mm, "end": v(6.7, 46.1) * mm});
            skPoint(sketch, "E198.startSnap0", {"position": v(3.35, 26.1) * mm});
            skLineSegment(sketch, "E199.MirrorCS", {"start": v(-20, 87.6) * mm, "end": v(-20, 84.6) * mm});
            skLineSegment(sketch, "E200.MirrorCS", {"start": v(-20, 84.6) * mm, "end": v(-12.19, 84.6) * mm});
            skLineSegment(sketch, "E201.MirrorCS", {"start": v(-12.19, 87.6) * mm, "end": v(-20, 87.6) * mm});
            skLineSegment(sketch, "E202.MirrorCS", {"start": v(-12.19, 88.86) * mm, "end": v(-12.19, 87.6) * mm});
            skLineSegment(sketch, "E203.MirrorCS", {"start": v(-10.39, 83.36) * mm, "end": v(-10.39, 84.6) * mm});
            skLineSegment(sketch, "E204.MirrorCS", {"start": v(-12.19, 84.6) * mm, "end": v(-12.19, 83.36) * mm});
            skLineSegment(sketch, "E205.MirrorCS", {"start": v(-12.19, 83.36) * mm, "end": v(-10.39, 83.36) * mm});
            skLineSegment(sketch, "E206.MirrorCS", {"start": v(-10.39, 88.86) * mm, "end": v(-12.19, 88.86) * mm});
            skLineSegment(sketch, "E207.MirrorCS", {"start": v(-10.39, 87.6) * mm, "end": v(-10.39, 88.86) * mm});
            skLineSegment(sketch, "E208.MirrorCS", {"start": v(0, 87.6) * mm, "end": v(-10.39, 87.6) * mm});
            skLineSegment(sketch, "E209.MirrorCS", {"start": v(-10.39, 84.6) * mm, "end": v(0, 84.6) * mm});
            skLineSegment(sketch, "E210.MirrorCS", {"start": v(-8.55, 155.62) * mm, "end": v(-8.55, 154.54) * mm});
            skLineSegment(sketch, "E211.MirrorCS", {"start": v(-6.75, 155.62) * mm, "end": v(-8.55, 155.62) * mm});
            skLineSegment(sketch, "E212.MirrorCS", {"start": v(-6.75, 154.54) * mm, "end": v(-6.75, 155.62) * mm});
            skLineSegment(sketch, "E213.MirrorCS", {"start": v(-8.55, 154.54) * mm, "end": v(-20, 154.54) * mm});
            skLineSegment(sketch, "E214.MirrorCS", {"start": v(-20, 154.54) * mm, "end": v(-20, 151.54) * mm});
            skLineSegment(sketch, "E215.MirrorCS", {"start": v(-20, 151.54) * mm, "end": v(-8.55, 151.54) * mm});
            skLineSegment(sketch, "E216.MirrorCS", {"start": v(-8.55, 151.54) * mm, "end": v(-8.55, 150.12) * mm});
            skLineSegment(sketch, "E217.MirrorCS", {"start": v(-8.55, 150.12) * mm, "end": v(-6.75, 150.12) * mm});
            skLineSegment(sketch, "E218.MirrorCS", {"start": v(-6.75, 150.12) * mm, "end": v(-6.75, 151.54) * mm});
            skLineSegment(sketch, "E219.MirrorCS", {"start": v(-6.75, 151.54) * mm, "end": v(0, 151.54) * mm});
            skLineSegment(sketch, "E220.MirrorCS", {"start": v(0, 154.54) * mm, "end": v(-6.75, 154.54) * mm});
            skLineSegment(sketch, "E221.MirrorCS", {"start": v(0, 222.2) * mm, "end": v(0, 154.54) * mm});
            skLineSegment(sketch, "E222.MirrorCS", {"start": v(0, 151.54) * mm, "end": v(0, 126.1) * mm});
            skLineSegment(sketch, "E223.MirrorCS", {"start": v(0, 126.1) * mm, "end": v(6.7, 126.1) * mm});
            skLineSegment(sketch, "E224.MirrorCS", {"start": v(6.7, 106.1) * mm, "end": v(0, 106.1) * mm});
            skLineSegment(sketch, "E225.MirrorCS", {"start": v(0, 106.1) * mm, "end": v(0, 87.6) * mm});
            skLineSegment(sketch, "E226.MirrorCS", {"start": v(0, 84.6) * mm, "end": v(0, 66.1) * mm});
            skLineSegment(sketch, "E227.MirrorCS", {"start": v(0, 66.1) * mm, "end": v(6.7, 66.1) * mm});
            skLineSegment(sketch, "E228.MirrorCS", {"start": v(6.7, 46.1) * mm, "end": v(0, 46.1) * mm});
            skLineSegment(sketch, "E229.MirrorCS", {"start": v(0, 46.1) * mm, "end": v(0, 26.1) * mm});
            skLineSegment(sketch, "E230.MirrorCS", {"start": v(-61.5, 37.9) * mm, "end": v(-62.75, 37.9) * mm});
            skLineSegment(sketch, "E231.MirrorCS", {"start": v(-11.5, 37.9) * mm, "end": v(-12.75, 37.9) * mm});
            skLineSegment(sketch, "E232.MirrorCS", {"start": v(-12.75, 36.1) * mm, "end": v(-11.5, 36.1) * mm});
            skLineSegment(sketch, "E233.MirrorCS", {"start": v(-62.75, 36.1) * mm, "end": v(-61.5, 36.1) * mm});
            skLineSegment(sketch, "E234.MirrorCS", {"start": v(-12.75, 37.9) * mm, "end": v(-12.75, 36.1) * mm});
            skLineSegment(sketch, "E235.MirrorCS", {"start": v(-62.75, 37.9) * mm, "end": v(-62.75, 36.1) * mm});
            skLineSegment(sketch, "E236.MirrorCS", {"start": v(-7.25, 36.1) * mm, "end": v(-7.25, 37.9) * mm});
            skLineSegment(sketch, "E237.MirrorCS", {"start": v(-8.5, 36.1) * mm, "end": v(-7.25, 36.1) * mm});
            skLineSegment(sketch, "E238.MirrorCS", {"start": v(-57.25, 36.1) * mm, "end": v(-57.25, 37.9) * mm});
            skLineSegment(sketch, "E239.MirrorCS", {"start": v(-7.25, 37.9) * mm, "end": v(-8.5, 37.9) * mm});
            skLineSegment(sketch, "E240.MirrorCS", {"start": v(-58.5, 36.1) * mm, "end": v(-57.25, 36.1) * mm});
            skLineSegment(sketch, "E241.MirrorCS", {"start": v(-57.25, 37.9) * mm, "end": v(-58.5, 37.9) * mm});
            skLineSegment(sketch, "E242.MirrorCS", {"start": v(-8.5, 46.1) * mm, "end": v(-11.5, 46.1) * mm});
            skLineSegment(sketch, "E243.MirrorCS", {"start": v(-58.5, 46.1) * mm, "end": v(-61.5, 46.1) * mm});
            skLineSegment(sketch, "E244.MirrorCS", {"start": v(0, 26.1) * mm, "end": v(-8.5, 26.1) * mm});
            skLineSegment(sketch, "E245.MirrorCS", {"start": v(-80, 26.1) * mm, "end": v(-80, 19.4) * mm});
            skLineSegment(sketch, "E246.MirrorCS", {"start": v(-100, 26.1) * mm, "end": v(-120, 26.1) * mm});
            skLineSegment(sketch, "E247.MirrorCS", {"start": v(-11.5, 36.1) * mm, "end": v(-11.5, 26.1) * mm});
            skLineSegment(sketch, "E248.MirrorCS", {"start": v(-20, 26.1) * mm, "end": v(-20, 19.4) * mm});
            skLineSegment(sketch, "E249.MirrorCS", {"start": v(-40, 26.1) * mm, "end": v(-58.5, 26.1) * mm});
            skLineSegment(sketch, "E250.MirrorCS", {"start": v(-61.5, 36.1) * mm, "end": v(-61.5, 26.1) * mm});
            skLineSegment(sketch, "E251.MirrorCS", {"start": v(-58.5, 26.1) * mm, "end": v(-58.5, 36.1) * mm});
            skLineSegment(sketch, "E252.MirrorCS", {"start": v(-80, 19.4) * mm, "end": v(-100, 19.4) * mm});
            skLineSegment(sketch, "E253.MirrorCS", {"start": v(-61.5, 46.1) * mm, "end": v(-61.5, 37.9) * mm});
            skLineSegment(sketch, "E254.MirrorCS", {"start": v(-8.5, 26.1) * mm, "end": v(-8.5, 36.1) * mm});
            skLineSegment(sketch, "E255.MirrorCS", {"start": v(-120, 26.1) * mm, "end": v(0, 222.2) * mm});
            skLineSegment(sketch, "E256.MirrorCS", {"start": v(-61.5, 26.1) * mm, "end": v(-80, 26.1) * mm});
            skLineSegment(sketch, "E257.MirrorCS", {"start": v(-100, 19.4) * mm, "end": v(-100, 26.1) * mm});
            skLineSegment(sketch, "E258.MirrorCS", {"start": v(-58.5, 37.9) * mm, "end": v(-58.5, 46.1) * mm});
            skLineSegment(sketch, "E259.MirrorCS", {"start": v(-40, 19.4) * mm, "end": v(-40, 26.1) * mm});
            skLineSegment(sketch, "E260.MirrorCS", {"start": v(-8.5, 37.9) * mm, "end": v(-8.5, 46.1) * mm});
            skLineSegment(sketch, "E261.MirrorCS", {"start": v(-20, 19.4) * mm, "end": v(-40, 19.4) * mm});
            skLineSegment(sketch, "E262.MirrorCS", {"start": v(-11.5, 46.1) * mm, "end": v(-11.5, 37.9) * mm});
            skLineSegment(sketch, "E263.MirrorCS", {"start": v(-11.5, 26.1) * mm, "end": v(-20, 26.1) * mm});
            skLineSegment(sketch, "E264", {"start": v(6.7, 46.1) * mm, "end": v(6.7, 66.1) * mm});
            skLineSegment(sketch, "E265", {"start": v(6.7, 106.1) * mm, "end": v(6.7, 126.1) * mm});
            skSolve(sketch);
        }
        {
            var Q0;
            Q0 = qSketchRegion(id + "F6", true);
            extrude(context, id + "F7", {"entities" : qUnion([Q0]), "depth" : 6.7 * mm});
        }
        {
            var Q0;
            Q0=makeQuery(id+"F1.opExtrude","SWEPT_FACE",FACE,{"disambiguationData":[OSD([sQuery(id+"F0.wireOp",EDGE,"E7")])]});
            var sketch = newSketch(context, id + "F8", { "sketchPlane" : qUnion([Q0])});
            skLineSegment(sketch, "E266.0", {"start": v(-247, 6.7) * mm, "end": v(-247, 0) * mm});
            skLineSegment(sketch, "E266.1", {"start": v(-137.86, 126.7) * mm, "end": v(-131.16, 126.7) * mm});
            skLineSegment(sketch, "E267.0", {"start": v(-163.56, -120) * mm, "end": v(-156.86, -120) * mm});
            skLineSegment(sketch, "E268.0", {"start": v(-55.14, 6.7) * mm, "end": v(-55.14, 0) * mm, "construction": true});
            skLineSegment(sketch, "E269.0", {"start": v(19.86, 6.7) * mm, "end": v(19.86, 0) * mm, "construction": true});
            skLineSegment(sketch, "E270", {"start": v(-55.14, 3.35) * mm, "end": v(19.86, 3.35) * mm, "construction": true});
            skLineSegment(sketch, "E271", {"start": v(-17.64, 3.35) * mm, "end": v(-17.64, -149.87) * mm, "construction": true});
            skLineSegment(sketch, "E272", {"start": v(-163.56, -120) * mm, "end": v(-247, 0) * mm});
            skLineSegment(sketch, "E273", {"start": v(-247, 6.7) * mm, "end": v(-137.86, 126.7) * mm});
            skLineSegment(sketch, "E274", {"start": v(-156.86, -120) * mm, "end": v(-17.64, -120) * mm});
            skLineSegment(sketch, "E275", {"start": v(-131.16, 126.7) * mm, "end": v(-17.64, 126.7) * mm});
            skLineSegment(sketch, "E276.0.0", {"start": v(-222, 0) * mm, "end": v(-202, 0) * mm});
            skLineSegment(sketch, "E276.0.1", {"start": v(-202, 0) * mm, "end": v(-202, 6.7) * mm});
            skLineSegment(sketch, "E276.0.2", {"start": v(-202, 6.7) * mm, "end": v(-222, 6.7) * mm});
            skLineSegment(sketch, "E276.0.3", {"start": v(-222, 6.7) * mm, "end": v(-222, 0) * mm});
            skLineSegment(sketch, "E277.0.0", {"start": v(-192, 0) * mm, "end": v(-172, 0) * mm});
            skLineSegment(sketch, "E277.0.1", {"start": v(-172, 0) * mm, "end": v(-172, 6.7) * mm});
            skLineSegment(sketch, "E277.0.2", {"start": v(-172, 6.7) * mm, "end": v(-192, 6.7) * mm});
            skLineSegment(sketch, "E277.0.3", {"start": v(-192, 6.7) * mm, "end": v(-192, 0) * mm});
            skLineSegment(sketch, "E278.0.0", {"start": v(-122, 0) * mm, "end": v(-102, 0) * mm});
            skLineSegment(sketch, "E278.0.1", {"start": v(-102, 0) * mm, "end": v(-102, 6.7) * mm});
            skLineSegment(sketch, "E278.0.2", {"start": v(-102, 6.7) * mm, "end": v(-122, 6.7) * mm});
            skLineSegment(sketch, "E278.0.3", {"start": v(-122, 6.7) * mm, "end": v(-122, 0) * mm});
            skLineSegment(sketch, "E279.0.0", {"start": v(-92, 0) * mm, "end": v(-72, 0) * mm});
            skLineSegment(sketch, "E279.0.1", {"start": v(-72, 0) * mm, "end": v(-72, 6.7) * mm});
            skLineSegment(sketch, "E279.0.2", {"start": v(-72, 6.7) * mm, "end": v(-92, 6.7) * mm});
            skLineSegment(sketch, "E279.0.3", {"start": v(-92, 6.7) * mm, "end": v(-92, 0) * mm});
            skLineSegment(sketch, "E280.0", {"start": v(-198.5, 6.7) * mm, "end": v(-198.5, 0) * mm, "construction": true});
            skLineSegment(sketch, "E281.0", {"start": v(-195.5, 6.7) * mm, "end": v(-195.5, 0) * mm, "construction": true});
            skLineSegment(sketch, "E282.0", {"start": v(-148.5, 6.7) * mm, "end": v(-148.5, 0) * mm, "construction": true});
            skLineSegment(sketch, "E283.0", {"start": v(-145.5, 6.7) * mm, "end": v(-145.5, 0) * mm, "construction": true});
            skLineSegment(sketch, "E284", {"start": v(-198.5, 3.35) * mm, "end": v(-195.5, 3.35) * mm, "construction": true});
            skCircle(sketch, "E285", {"center": v(-197, 3.35) * mm, "radius": 1.5 * mm});
            skLineSegment(sketch, "E286", {"start": v(-148.5, 3.35) * mm, "end": v(-145.5, 3.35) * mm, "construction": true});
            skCircle(sketch, "E287", {"center": v(-147, 3.35) * mm, "radius": 1.5 * mm});
            skLineSegment(sketch, "E288.MirrorCS", {"start": v(160.22, 6.7) * mm, "end": v(160.22, 0) * mm, "construction": true});
            skCircle(sketch, "E289.MirrorC", {"center": v(161.72, 3.35) * mm, "radius": 1.5 * mm});
            skLineSegment(sketch, "E290.MirrorCS", {"start": v(163.22, 3.35) * mm, "end": v(160.22, 3.35) * mm, "construction": true});
            skLineSegment(sketch, "E291.MirrorCS", {"start": v(163.22, 6.7) * mm, "end": v(163.22, 0) * mm, "construction": true});
            skLineSegment(sketch, "E292.MirrorCS", {"start": v(156.72, 6.7) * mm, "end": v(156.72, 0) * mm});
            skLineSegment(sketch, "E293.MirrorCS", {"start": v(166.72, 0) * mm, "end": v(166.72, 6.7) * mm});
            skLineSegment(sketch, "E294.MirrorCS", {"start": v(110.22, 6.7) * mm, "end": v(110.22, 0) * mm, "construction": true});
            skLineSegment(sketch, "E295.MirrorCS", {"start": v(56.72, 6.7) * mm, "end": v(56.72, 0) * mm});
            skLineSegment(sketch, "E296.MirrorCS", {"start": v(113.22, 3.35) * mm, "end": v(110.22, 3.35) * mm, "construction": true});
            skLineSegment(sketch, "E297.MirrorCS", {"start": v(36.72, 0) * mm, "end": v(36.72, 6.7) * mm});
            skLineSegment(sketch, "E298.MirrorCS", {"start": v(186.72, 6.7) * mm, "end": v(186.72, 0) * mm});
            skLineSegment(sketch, "E299.MirrorCS", {"start": v(211.72, 6.7) * mm, "end": v(211.72, 0) * mm});
            skLineSegment(sketch, "E300.MirrorCS", {"start": v(102.57, 126.7) * mm, "end": v(95.87, 126.7) * mm});
            skCircle(sketch, "E301.MirrorC", {"center": v(111.72, 3.35) * mm, "radius": 1.5 * mm});
            skLineSegment(sketch, "E302.MirrorCS", {"start": v(66.72, 0) * mm, "end": v(66.72, 6.7) * mm});
            skLineSegment(sketch, "E303.MirrorCS", {"start": v(113.22, 6.7) * mm, "end": v(113.22, 0) * mm, "construction": true});
            skLineSegment(sketch, "E304.MirrorCS", {"start": v(86.72, 6.7) * mm, "end": v(86.72, 0) * mm});
            skLineSegment(sketch, "E305.MirrorCS", {"start": v(128.27, -120) * mm, "end": v(121.57, -120) * mm});
            skLineSegment(sketch, "E306.MirrorCS", {"start": v(136.72, 0) * mm, "end": v(136.72, 6.7) * mm});
            skLineSegment(sketch, "E307.MirrorCS", {"start": v(86.72, 0) * mm, "end": v(66.72, 0) * mm});
            skLineSegment(sketch, "E308.MirrorCS", {"start": v(66.72, 6.7) * mm, "end": v(86.72, 6.7) * mm});
            skLineSegment(sketch, "E309.MirrorCS", {"start": v(136.72, 6.7) * mm, "end": v(156.72, 6.7) * mm});
            skLineSegment(sketch, "E310.MirrorCS", {"start": v(56.72, 0) * mm, "end": v(36.72, 0) * mm});
            skLineSegment(sketch, "E311.MirrorCS", {"start": v(166.72, 6.7) * mm, "end": v(186.72, 6.7) * mm});
            skLineSegment(sketch, "E312.MirrorCS", {"start": v(156.72, 0) * mm, "end": v(136.72, 0) * mm});
            skLineSegment(sketch, "E313.MirrorCS", {"start": v(211.72, 6.7) * mm, "end": v(102.57, 126.7) * mm});
            skLineSegment(sketch, "E314.MirrorCS", {"start": v(36.72, 6.7) * mm, "end": v(56.72, 6.7) * mm});
            skLineSegment(sketch, "E315.MirrorCS", {"start": v(121.57, -120) * mm, "end": v(-17.64, -120) * mm});
            skLineSegment(sketch, "E316.MirrorCS", {"start": v(128.27, -120) * mm, "end": v(211.72, 0) * mm});
            skLineSegment(sketch, "E317.MirrorCS", {"start": v(95.87, 126.7) * mm, "end": v(-17.64, 126.7) * mm});
            skLineSegment(sketch, "E318.MirrorCS", {"start": v(186.72, 0) * mm, "end": v(166.72, 0) * mm});
            skLineSegment(sketch, "E319.0.0", {"start": v(-156.86, -100) * mm, "end": v(-156.86, -80) * mm});
            skLineSegment(sketch, "E319.0.1", {"start": v(-156.86, -80) * mm, "end": v(-163.56, -80) * mm});
            skLineSegment(sketch, "E319.0.2", {"start": v(-163.56, -80) * mm, "end": v(-163.56, -100) * mm});
            skLineSegment(sketch, "E319.0.3", {"start": v(-163.56, -100) * mm, "end": v(-156.86, -100) * mm});
            skLineSegment(sketch, "E320.0.0", {"start": v(-156.86, -40) * mm, "end": v(-156.86, -20) * mm});
            skLineSegment(sketch, "E320.0.1", {"start": v(-156.86, -20) * mm, "end": v(-163.56, -20) * mm});
            skLineSegment(sketch, "E320.0.2", {"start": v(-163.56, -20) * mm, "end": v(-163.56, -40) * mm});
            skLineSegment(sketch, "E320.0.3", {"start": v(-163.56, -40) * mm, "end": v(-156.86, -40) * mm});
            skLineSegment(sketch, "E321.0.0", {"start": v(-131.16, 26.7) * mm, "end": v(-131.16, 46.7) * mm});
            skLineSegment(sketch, "E321.0.1", {"start": v(-131.16, 46.7) * mm, "end": v(-137.86, 46.7) * mm});
            skLineSegment(sketch, "E321.0.2", {"start": v(-137.86, 46.7) * mm, "end": v(-137.86, 26.7) * mm});
            skLineSegment(sketch, "E321.0.3", {"start": v(-137.86, 26.7) * mm, "end": v(-131.16, 26.7) * mm});
            skLineSegment(sketch, "E322.0.0", {"start": v(-131.16, 86.7) * mm, "end": v(-131.16, 106.7) * mm});
            skLineSegment(sketch, "E322.0.1", {"start": v(-131.16, 106.7) * mm, "end": v(-137.86, 106.7) * mm});
            skLineSegment(sketch, "E322.0.2", {"start": v(-137.86, 106.7) * mm, "end": v(-137.86, 86.7) * mm});
            skLineSegment(sketch, "E322.0.3", {"start": v(-137.86, 86.7) * mm, "end": v(-131.16, 86.7) * mm});
            skLineSegment(sketch, "E323.0", {"start": v(-137.86, 68.2) * mm, "end": v(-131.16, 68.2) * mm, "construction": true});
            skLineSegment(sketch, "E324.0", {"start": v(-137.86, 65.2) * mm, "end": v(-131.16, 65.2) * mm, "construction": true});
            skLineSegment(sketch, "E325.0", {"start": v(-137.86, 15.2) * mm, "end": v(-131.16, 15.2) * mm, "construction": true});
            skLineSegment(sketch, "E326.0", {"start": v(-137.86, 18.2) * mm, "end": v(-131.16, 18.2) * mm, "construction": true});
            skLineSegment(sketch, "E327.0", {"start": v(-163.56, -11.5) * mm, "end": v(-156.86, -11.5) * mm, "construction": true});
            skLineSegment(sketch, "E328.0", {"start": v(-163.56, -8.5) * mm, "end": v(-156.86, -8.5) * mm, "construction": true});
            skLineSegment(sketch, "E329.0", {"start": v(-163.56, -61.5) * mm, "end": v(-156.86, -61.5) * mm, "construction": true});
            skLineSegment(sketch, "E330.0", {"start": v(-163.56, -58.5) * mm, "end": v(-156.86, -58.5) * mm, "construction": true});
            skLineSegment(sketch, "E331", {"start": v(-160.2, -61.5) * mm, "end": v(-160.2, -58.5) * mm, "construction": true});
            skLineSegment(sketch, "E332", {"start": v(-160.2, -11.5) * mm, "end": v(-160.2, -8.5) * mm, "construction": true});
            skLineSegment(sketch, "E333", {"start": v(-134.5, 15.2) * mm, "end": v(-134.5, 18.2) * mm, "construction": true});
            skLineSegment(sketch, "E334", {"start": v(-134.5, 65.2) * mm, "end": v(-134.5, 68.2) * mm, "construction": true});
            skCircle(sketch, "E335", {"center": v(-134.5, 66.7) * mm, "radius": 1.5 * mm});
            skCircle(sketch, "E336", {"center": v(-134.5, 16.7) * mm, "radius": 1.5 * mm});
            skCircle(sketch, "E337", {"center": v(-160.2, -10) * mm, "radius": 1.5 * mm});
            skCircle(sketch, "E338", {"center": v(-160.2, -60) * mm, "radius": 1.5 * mm});
            skLineSegment(sketch, "E339.MirrorCS", {"start": v(124.92, -61.5) * mm, "end": v(124.92, -58.5) * mm, "construction": true});
            skLineSegment(sketch, "E340.MirrorCS", {"start": v(124.92, -11.5) * mm, "end": v(124.92, -8.5) * mm, "construction": true});
            skLineSegment(sketch, "E341.MirrorCS", {"start": v(128.27, -80) * mm, "end": v(128.27, -100) * mm});
            skCircle(sketch, "E342.MirrorC", {"center": v(124.92, -60) * mm, "radius": 1.5 * mm});
            skLineSegment(sketch, "E343.MirrorCS", {"start": v(128.27, -11.5) * mm, "end": v(121.57, -11.5) * mm, "construction": true});
            skLineSegment(sketch, "E344.MirrorCS", {"start": v(128.27, -8.5) * mm, "end": v(121.57, -8.5) * mm, "construction": true});
            skLineSegment(sketch, "E345.MirrorCS", {"start": v(128.27, -20) * mm, "end": v(128.27, -40) * mm});
            skLineSegment(sketch, "E346.MirrorCS", {"start": v(121.57, -80) * mm, "end": v(128.27, -80) * mm});
            skLineSegment(sketch, "E347.MirrorCS", {"start": v(121.57, -100) * mm, "end": v(121.57, -80) * mm});
            skCircle(sketch, "E348.MirrorC", {"center": v(124.92, -10) * mm, "radius": 1.5 * mm});
            skLineSegment(sketch, "E349.MirrorCS", {"start": v(128.27, -58.5) * mm, "end": v(121.57, -58.5) * mm, "construction": true});
            skLineSegment(sketch, "E350.MirrorCS", {"start": v(128.27, -61.5) * mm, "end": v(121.57, -61.5) * mm, "construction": true});
            skLineSegment(sketch, "E351.MirrorCS", {"start": v(121.57, -40) * mm, "end": v(121.57, -20) * mm});
            skLineSegment(sketch, "E352.MirrorCS", {"start": v(121.57, -20) * mm, "end": v(128.27, -20) * mm});
            skLineSegment(sketch, "E353.MirrorCS", {"start": v(128.27, -100) * mm, "end": v(121.57, -100) * mm});
            skLineSegment(sketch, "E354.MirrorCS", {"start": v(128.27, -40) * mm, "end": v(121.57, -40) * mm});
            skLineSegment(sketch, "E355.MirrorCS", {"start": v(99.22, 65.2) * mm, "end": v(99.22, 68.2) * mm, "construction": true});
            skLineSegment(sketch, "E356.MirrorCS", {"start": v(99.22, 15.2) * mm, "end": v(99.22, 18.2) * mm, "construction": true});
            skLineSegment(sketch, "E357.MirrorCS", {"start": v(102.57, 106.7) * mm, "end": v(102.57, 86.7) * mm});
            skLineSegment(sketch, "E358.MirrorCS", {"start": v(102.57, 46.7) * mm, "end": v(102.57, 26.7) * mm});
            skCircle(sketch, "E359.MirrorC", {"center": v(99.22, 66.7) * mm, "radius": 1.5 * mm});
            skLineSegment(sketch, "E360.MirrorCS", {"start": v(102.57, 86.7) * mm, "end": v(95.87, 86.7) * mm});
            skLineSegment(sketch, "E361.MirrorCS", {"start": v(95.87, 86.7) * mm, "end": v(95.87, 106.7) * mm});
            skLineSegment(sketch, "E362.MirrorCS", {"start": v(102.57, 18.2) * mm, "end": v(95.87, 18.2) * mm, "construction": true});
            skCircle(sketch, "E363.MirrorC", {"center": v(99.22, 16.7) * mm, "radius": 1.5 * mm});
            skLineSegment(sketch, "E364.MirrorCS", {"start": v(102.57, 26.7) * mm, "end": v(95.87, 26.7) * mm});
            skLineSegment(sketch, "E365.MirrorCS", {"start": v(95.87, 26.7) * mm, "end": v(95.87, 46.7) * mm});
            skLineSegment(sketch, "E366.MirrorCS", {"start": v(95.87, 46.7) * mm, "end": v(102.57, 46.7) * mm});
            skLineSegment(sketch, "E367.MirrorCS", {"start": v(102.57, 15.2) * mm, "end": v(95.87, 15.2) * mm, "construction": true});
            skLineSegment(sketch, "E368.MirrorCS", {"start": v(95.87, 106.7) * mm, "end": v(102.57, 106.7) * mm});
            skLineSegment(sketch, "E369.MirrorCS", {"start": v(102.57, 65.2) * mm, "end": v(95.87, 65.2) * mm, "construction": true});
            skLineSegment(sketch, "E370.MirrorCS", {"start": v(102.57, 68.2) * mm, "end": v(95.87, 68.2) * mm, "construction": true});
            skSolve(sketch);
        }
        {
            var Q0;
            Q0 = qSketchRegion(id + "F8", true);
            extrude(context, id + "F9", {"entities" : qUnion([Q0]), "depth" : 6.7 * mm});
        }
    });
